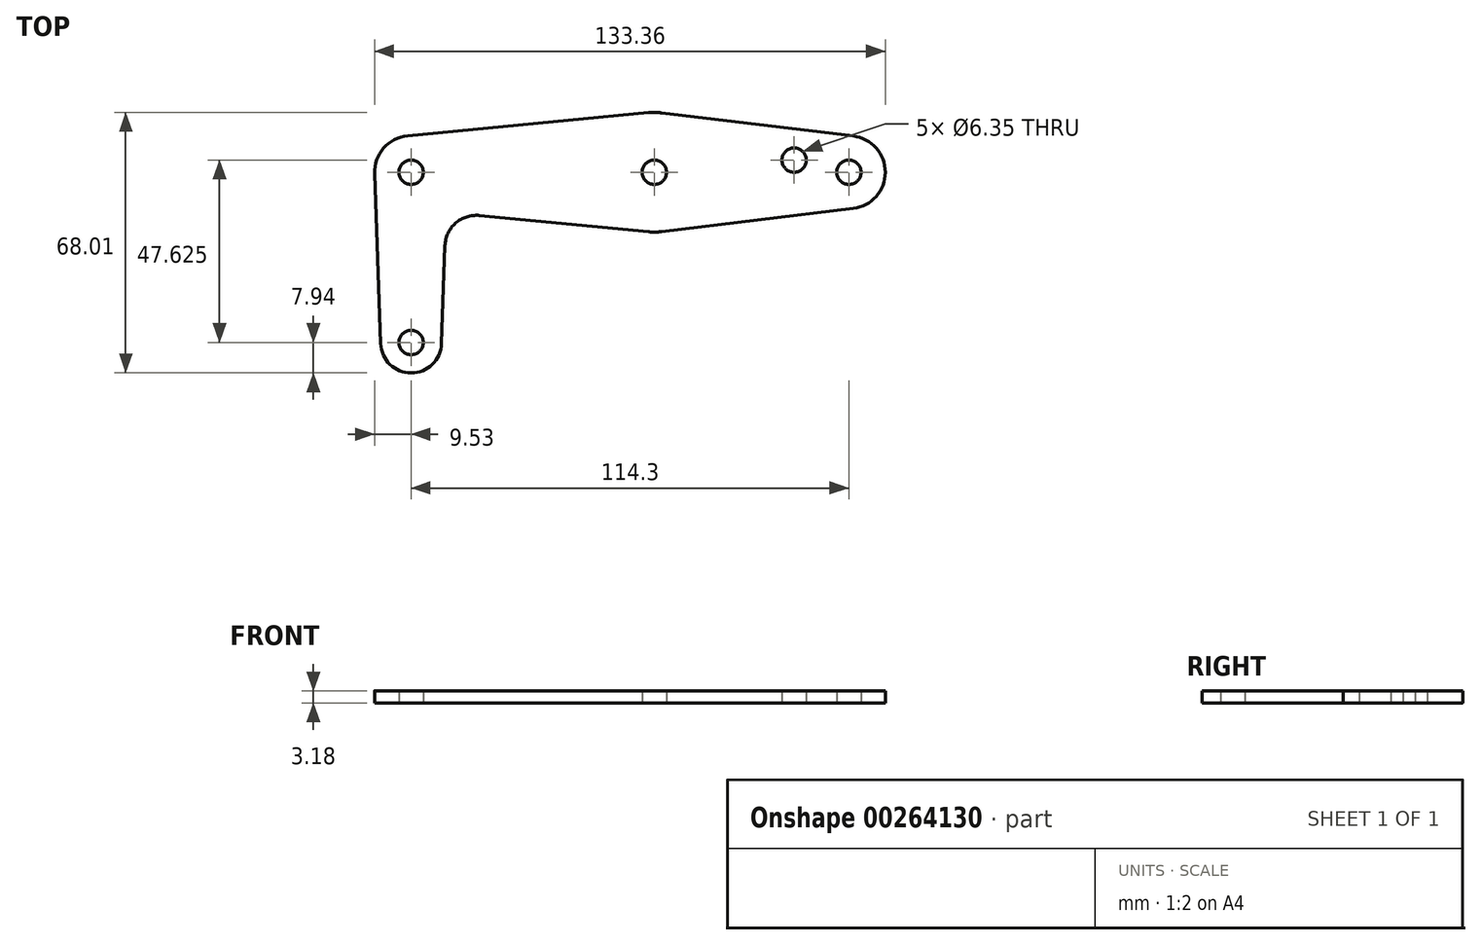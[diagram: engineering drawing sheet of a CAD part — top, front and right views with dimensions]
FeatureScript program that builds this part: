
annotation { "Feature Type Name" : "Feature", "Feature Type Description" : "" }
export const myFeature = defineFeature(function(context is Context, id is Id, definition is map)
    precondition{}
    {
        {
            var Q0;
            Q0=qCreatedBy(makeId("Top.planeOp"),FACE);
            var sketch = newSketch(context, id + "F0", { "sketchPlane" : qUnion([Q0])});
            skLineSegment(sketch, "E0", {"start": v(114.3, 0) * mm, "end": v(0, 0) * mm, "construction": true});
            skLineSegment(sketch, "E1", {"start": v(0, 0) * mm, "end": v(0, -44.45) * mm, "construction": true});
            skCircle(sketch, "E2", {"center": v(0, -44.45) * mm, "radius": 7.94 * mm});
            skCircle(sketch, "E3", {"center": v(0, 0) * mm, "radius": 9.53 * mm});
            skCircle(sketch, "E4", {"center": v(114.3, 0) * mm, "radius": 9.53 * mm});
            skCircle(sketch, "E5", {"center": v(63.5, 0) * mm, "radius": 3.18 * mm});
            skCircle(sketch, "E6", {"center": v(0, 0) * mm, "radius": 3.18 * mm});
            skCircle(sketch, "E7", {"center": v(0, -44.45) * mm, "radius": 3.18 * mm});
            skCircle(sketch, "E8", {"center": v(114.3, 0) * mm, "radius": 3.18 * mm});
            skCircle(sketch, "E9", {"center": v(100.01, 3.18) * mm, "radius": 3.18 * mm});
            skLineSegment(sketch, "E10", {"start": v(-9.52, -0.34) * mm, "end": v(-7.93, -44.73) * mm});
            skLineSegment(sketch, "E11", {"start": v(7.93, -44.73) * mm, "end": v(9.53, 0) * mm});
            skCircle(sketch, "E12", {"center": v(63.5, 0) * mm, "radius": 15.62 * mm});
            skLineSegment(sketch, "E13", {"start": v(-0.91, 9.48) * mm, "end": v(62, 15.55) * mm});
            skLineSegment(sketch, "E14", {"start": v(65.37, 15.5) * mm, "end": v(115.44, 9.46) * mm});
            skLineSegment(sketch, "E15", {"start": v(-0.91, -9.48) * mm, "end": v(62, -15.55) * mm});
            skLineSegment(sketch, "E16", {"start": v(65.37, -15.5) * mm, "end": v(115.44, -9.46) * mm});
            skSolve(sketch);
        }
        {
            var Q0;
            Q0 = qSketchRegion(id + "F0", true);
            extrude(context, id + "F1", {"entities" : qUnion([Q0]), "depth" : 3.17 * mm});
        }
        {
            var Q0;
            Q0=makeQuery(id+"F1.opExtrude","SWEPT_EDGE",EDGE,{"disambiguationData":[OSD([sQuery(id+"F0.wireOp",EDGE,"E11"),sQuery(id+"F0.wireOp",EDGE,"E15")])]});
            fillet(context, id + "F2", {"entities" : qUnion([Q0]), "radius" : 8.2 * mm, "tangentPropagation" : true, "allowEdgeOverflow" : false});
        }
    });
